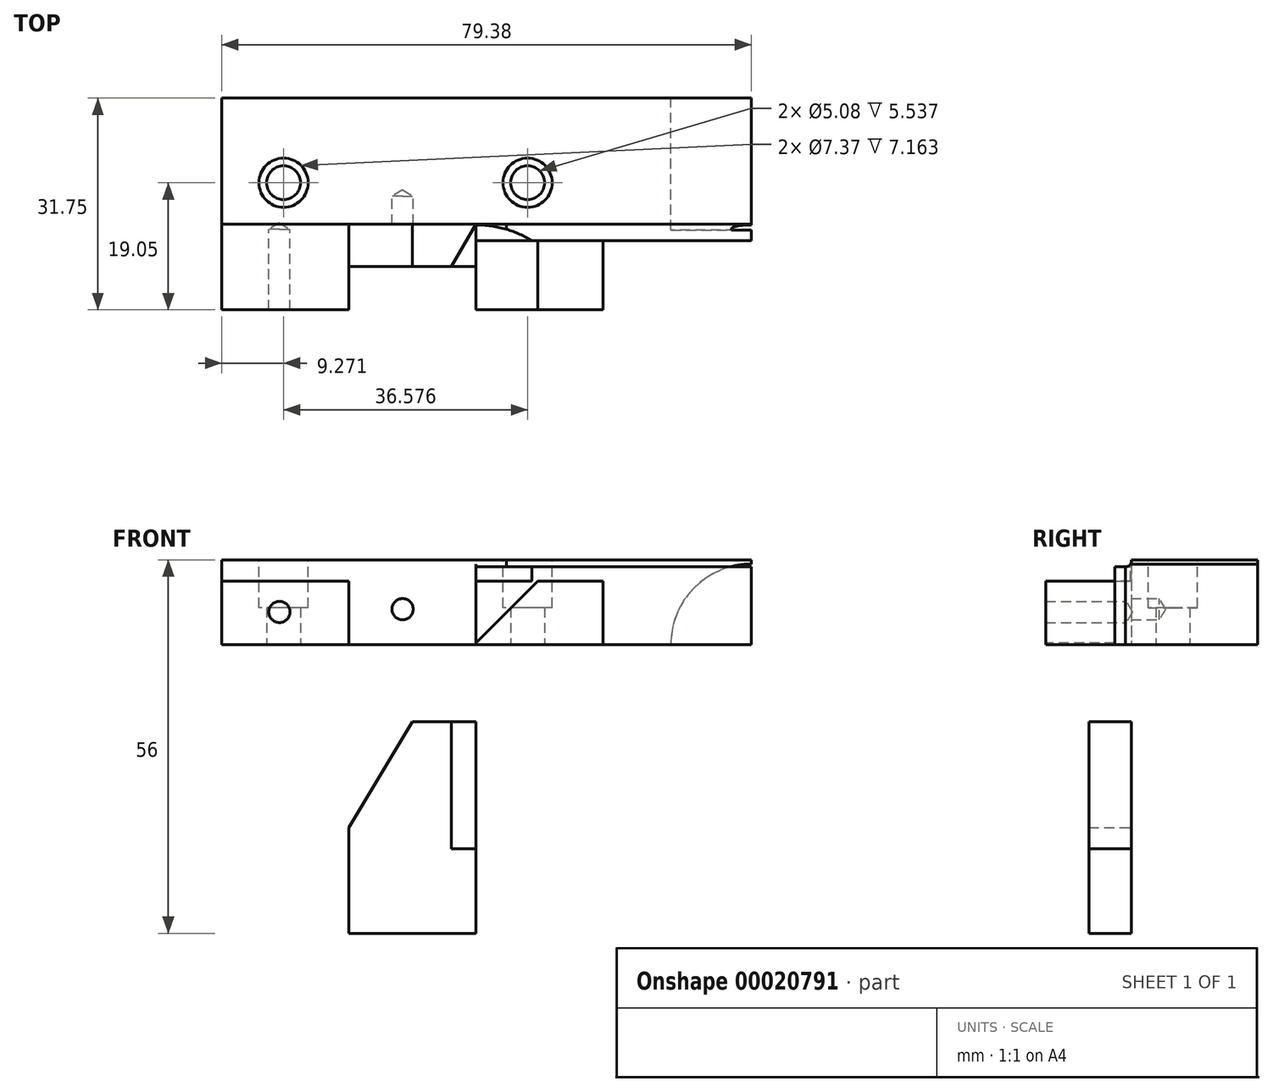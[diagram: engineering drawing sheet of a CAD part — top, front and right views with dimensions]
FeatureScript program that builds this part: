
annotation { "Feature Type Name" : "Feature", "Feature Type Description" : "" }
export const myFeature = defineFeature(function(context is Context, id is Id, definition is map)
    precondition{}
    {
        {
            var Q0;
            Q0=qCreatedBy(makeId("Top.planeOp"),FACE);
            var sketch = newSketch(context, id + "F0", { "sketchPlane" : qUnion([Q0])});
            skLineSegment(sketch, "E0", {"start": v(0, 0) * mm, "end": v(0, -31.75) * mm});
            skLineSegment(sketch, "E1", {"start": v(0, -31.75) * mm, "end": v(19.05, -31.75) * mm});
            skLineSegment(sketch, "E2", {"start": v(19.05, -31.75) * mm, "end": v(19.05, -18.92) * mm});
            skLineSegment(sketch, "E3", {"start": v(19.05, -18.92) * mm, "end": v(38.1, -18.92) * mm});
            skLineSegment(sketch, "E4", {"start": v(38.1, -18.92) * mm, "end": v(38.1, -31.75) * mm});
            skLineSegment(sketch, "E5", {"start": v(38.1, -31.75) * mm, "end": v(57.15, -31.75) * mm});
            skLineSegment(sketch, "E6", {"start": v(57.15, -31.75) * mm, "end": v(57.15, -21.39) * mm});
            skLineSegment(sketch, "E7", {"start": v(57.15, -21.39) * mm, "end": v(79.38, -21.39) * mm});
            skLineSegment(sketch, "E8", {"start": v(79.38, -21.39) * mm, "end": v(79.38, 0) * mm});
            skLineSegment(sketch, "E9", {"start": v(79.38, 0) * mm, "end": v(0, 0) * mm});
            skSolve(sketch);
        }
        {
            var Q0;
            Q0 = qSketchRegion(id + "F0", true);
            extrude(context, id + "F1", {"entities" : qUnion([Q0]), "depth" : 12.7 * mm});
        }
        {
            var Q0;
            Q0=makeQuery(id+"F1.opExtrude","CAP_FACE",FACE,{"disambiguationData":[OSD([sQuery(id+"F0.wireOp",EDGE,"E0"),sQuery(id+"F0.wireOp",EDGE,"E1"),sQuery(id+"F0.wireOp",EDGE,"E2"),sQuery(id+"F0.wireOp",EDGE,"E3"),sQuery(id+"F0.wireOp",EDGE,"E4"),sQuery(id+"F0.wireOp",EDGE,"E5"),sQuery(id+"F0.wireOp",EDGE,"E6"),sQuery(id+"F0.wireOp",EDGE,"E7"),sQuery(id+"F0.wireOp",EDGE,"E8"),sQuery(id+"F0.wireOp",EDGE,"E9")])],"isStart":false});
            var sketch = newSketch(context, id + "F2", { "sketchPlane" : qUnion([Q0])});
            skLineSegment(sketch, "E10.bottom", {"start": v(0, -31.75) * mm, "end": v(19.05, -31.75) * mm});
            skLineSegment(sketch, "E10.top", {"start": v(0, -18.92) * mm, "end": v(19.05, -18.92) * mm});
            skLineSegment(sketch, "E10.left", {"start": v(0, -31.75) * mm, "end": v(0, -18.92) * mm});
            skLineSegment(sketch, "E10.right", {"start": v(19.05, -31.75) * mm, "end": v(19.05, -18.92) * mm});
            skSolve(sketch);
        }
        {
            var Q0;
            Q0 = qSketchRegion(id + "F2", true);
            extrude(context, id + "F3", {"entities" : qUnion([Q0]), "operationType" : NewBodyOperationType.REMOVE, "oppositeDirection" : true, "depth" : 3.17 * mm});
        }
        {
            var Q0;
            Q0=makeQuery(id+"F1.opExtrude","CAP_FACE",FACE,{"disambiguationData":[OSD([sQuery(id+"F0.wireOp",EDGE,"E0"),sQuery(id+"F0.wireOp",EDGE,"E1"),sQuery(id+"F0.wireOp",EDGE,"E2"),sQuery(id+"F0.wireOp",EDGE,"E3"),sQuery(id+"F0.wireOp",EDGE,"E4"),sQuery(id+"F0.wireOp",EDGE,"E5"),sQuery(id+"F0.wireOp",EDGE,"E6"),sQuery(id+"F0.wireOp",EDGE,"E7"),sQuery(id+"F0.wireOp",EDGE,"E8"),sQuery(id+"F0.wireOp",EDGE,"E9")])],"isStart":false});
            var sketch = newSketch(context, id + "F4", { "sketchPlane" : qUnion([Q0])});
            skLineSegment(sketch, "E11.bottom", {"start": v(38.1, -31.75) * mm, "end": v(57.15, -31.75) * mm});
            skLineSegment(sketch, "E11.top", {"start": v(38.1, -21.39) * mm, "end": v(57.15, -21.39) * mm});
            skLineSegment(sketch, "E11.left", {"start": v(38.1, -31.75) * mm, "end": v(38.1, -21.39) * mm});
            skLineSegment(sketch, "E11.right", {"start": v(57.15, -31.75) * mm, "end": v(57.15, -21.39) * mm});
            skSolve(sketch);
        }
        {
            var Q0;
            Q0 = qSketchRegion(id + "F4", true);
            extrude(context, id + "F5", {"entities" : qUnion([Q0]), "operationType" : NewBodyOperationType.REMOVE, "oppositeDirection" : true, "depth" : 3.17 * mm});
        }
        {
            var Q0;
            Q0=makeQuery(id+"F1.opExtrude","SWEPT_FACE",FACE,{"disambiguationData":[OSD([sQuery(id+"F0.wireOp",EDGE,"E5")])]});
            var sketch = newSketch(context, id + "F6", { "sketchPlane" : qUnion([Q0])});
            skLineSegment(sketch, "E12", {"start": v(38.1, 0.25) * mm, "end": v(47.37, 9.53) * mm});
            skLineSegment(sketch, "E13", {"start": v(47.37, 9.53) * mm, "end": v(38.1, 9.53) * mm});
            skLineSegment(sketch, "E14", {"start": v(38.1, 9.53) * mm, "end": v(38.1, 0.25) * mm});
            skLineSegment(sketch, "E15", {"start": v(41.97, 0.25) * mm, "end": v(33.92, 0.25) * mm, "construction": true});
            skSolve(sketch);
        }
        {
            var Q0;
            Q0 = qSketchRegion(id + "F6", true);
            extrude(context, id + "F7", {"entities" : qUnion([Q0]), "operationType" : NewBodyOperationType.REMOVE, "oppositeDirection" : true, "depth" : 10.36 * mm});
        }
        {
            var Q0;
            Q0=makeQuery(id+"F1.opExtrude","CAP_FACE",FACE,{"disambiguationData":[OSD([sQuery(id+"F0.wireOp",EDGE,"E0"),sQuery(id+"F0.wireOp",EDGE,"E1"),sQuery(id+"F0.wireOp",EDGE,"E2"),sQuery(id+"F0.wireOp",EDGE,"E3"),sQuery(id+"F0.wireOp",EDGE,"E4"),sQuery(id+"F0.wireOp",EDGE,"E5"),sQuery(id+"F0.wireOp",EDGE,"E6"),sQuery(id+"F0.wireOp",EDGE,"E7"),sQuery(id+"F0.wireOp",EDGE,"E8"),sQuery(id+"F0.wireOp",EDGE,"E9")])],"isStart":false});
            var sketch = newSketch(context, id + "F8", { "sketchPlane" : qUnion([Q0])});
            skLineSegment(sketch, "E16.bottom", {"start": v(38.1, -21.39) * mm, "end": v(79.38, -21.39) * mm});
            skLineSegment(sketch, "E16.top", {"start": v(38.1, -18.92) * mm, "end": v(79.38, -18.92) * mm});
            skLineSegment(sketch, "E16.left", {"start": v(38.1, -21.39) * mm, "end": v(38.1, -18.92) * mm});
            skLineSegment(sketch, "E16.right", {"start": v(79.38, -21.39) * mm, "end": v(79.38, -18.92) * mm});
            skLineSegment(sketch, "E17.bottom", {"start": v(38.1, -18.92) * mm, "end": v(38.1, -18.92) * mm});
            skLineSegment(sketch, "E17.top", {"start": v(38.1, -18.92) * mm, "end": v(38.1, -18.92) * mm});
            skLineSegment(sketch, "E17.left", {"start": v(38.1, -18.92) * mm, "end": v(38.1, -18.92) * mm});
            skLineSegment(sketch, "E17.right", {"start": v(38.1, -18.92) * mm, "end": v(38.1, -18.92) * mm});
            skSolve(sketch);
        }
        {
            var Q0;
            Q0 = qSketchRegion(id + "F8", true);
            extrude(context, id + "F9", {"entities" : qUnion([Q0]), "operationType" : NewBodyOperationType.REMOVE, "oppositeDirection" : true, "depth" : 1.02 * mm});
        }
        {
            var Q0;
            Q0=makeQuery(id+"F1.opExtrude","SWEPT_FACE",FACE,{"disambiguationData":[OSD([sQuery(id+"F0.wireOp",EDGE,"E9")])]});
            var sketch = newSketch(context, id + "F10", { "sketchPlane" : qUnion([Q0])});
            skLineSegment(sketch, "E18", {"start": v(-85.5, 11.94) * mm, "end": v(-73.35, 11.94) * mm, "construction": true});
            skLineSegment(sketch, "E19", {"start": v(-67.1, -7.76) * mm, "end": v(-67.1, 3.98) * mm, "construction": true});
            skCircle(sketch, "E20", {"center": v(-79.38, 0) * mm, "radius": 12.07 * mm});
            skSolve(sketch);
        }
        {
            var Q0;
            Q0 = qSketchRegion(id + "F10", true);
            extrude(context, id + "F11", {"entities" : qUnion([Q0]), "operationType" : NewBodyOperationType.REMOVE, "oppositeDirection" : true, "depth" : 19.8 * mm});
        }
        {
            var Q0;
            Q0=makeQuery(id+"F9.boolean.opBoolean","COPY",FACE,{"derivedFrom":makeQuery(id+"F9.opExtrude","CAP_FACE",FACE,{"disambiguationData":[OSD([sQuery(id+"F8.wireOp",EDGE,"E16.bottom"),sQuery(id+"F8.wireOp",EDGE,"E16.top"),sQuery(id+"F8.wireOp",EDGE,"E16.left"),sQuery(id+"F8.wireOp",EDGE,"E16.right")])],"isStart":false})});
            var sketch = newSketch(context, id + "F12", { "sketchPlane" : qUnion([Q0])});
            skPoint(sketch, "E21.first.point", {"position": v(38.1, -18.92) * mm});
            skPoint(sketch, "E21.second.point", {"position": v(38.1, -52.5) * mm});
            skPoint(sketch, "E21.third.point", {"position": v(21.31, -36.1) * mm});
            skLineSegment(sketch, "E22", {"start": v(55.27, -29.27) * mm, "end": v(55.27, -36.3) * mm, "construction": true});
            skLineSegment(sketch, "E23", {"start": v(46.5, -17.5) * mm, "end": v(46.5, -27.25) * mm, "construction": true});
            skLineSegment(sketch, "E24", {"start": v(64.56, -31.75) * mm, "end": v(33.9, -31.75) * mm, "construction": true});
            skLineSegment(sketch, "E25", {"start": v(28.67, -21.39) * mm, "end": v(81.35, -21.39) * mm, "construction": true});
            skPoint(sketch, "E26.second.point", {"position": v(55.27, -31.75) * mm});
            skPoint(sketch, "E26.third.point", {"position": v(46.5, -21.39) * mm});
            skLineSegment(sketch, "E27", {"start": v(34, -19.02) * mm, "end": v(43.83, -19.02) * mm, "construction": true});
            skLineSegment(sketch, "E28", {"start": v(38.1, -20.68) * mm, "end": v(38.1, -16.21) * mm, "construction": true});
            skCircle(sketch, "E29", {"center": v(38.1, -35.17) * mm, "radius": 16.14 * mm});
            skSolve(sketch);
        }
        {
            var Q0;
            Q0 = qSketchRegion(id + "F12", true);
            var Q1;
            Q1=makeQuery(id+"F5.boolean.opBoolean","COPY",FACE,{"derivedFrom":makeQuery(id+"F5.opExtrude","CAP_FACE",FACE,{"disambiguationData":[OSD([sQuery(id+"F4.wireOp",EDGE,"E11.bottom"),sQuery(id+"F4.wireOp",EDGE,"E11.top"),sQuery(id+"F4.wireOp",EDGE,"E11.left"),sQuery(id+"F4.wireOp",EDGE,"E11.right")])],"isStart":false})});
            extrude(context, id + "F13", {"entities" : qUnion([Q0]), "operationType" : NewBodyOperationType.REMOVE, "endBound" : BoundingType.UP_TO_SURFACE, "oppositeDirection" : true, "endBoundEntityFace" : qUnion([Q1]), "depth" : 25.4 * mm});
        }
        {
            var Q0;
            Q0=makeQuery(id+"F1.opExtrude","CAP_FACE",FACE,{"disambiguationData":[OSD([sQuery(id+"F0.wireOp",EDGE,"E0"),sQuery(id+"F0.wireOp",EDGE,"E1"),sQuery(id+"F0.wireOp",EDGE,"E2"),sQuery(id+"F0.wireOp",EDGE,"E3"),sQuery(id+"F0.wireOp",EDGE,"E4"),sQuery(id+"F0.wireOp",EDGE,"E5"),sQuery(id+"F0.wireOp",EDGE,"E6"),sQuery(id+"F0.wireOp",EDGE,"E7"),sQuery(id+"F0.wireOp",EDGE,"E8"),sQuery(id+"F0.wireOp",EDGE,"E9")])],"isStart":true});
            var sketch = newSketch(context, id + "F14", { "sketchPlane" : qUnion([Q0])});
            skCircle(sketch, "E30", {"center": v(9.27, 12.7) * mm, "radius": 2.54 * mm});
            skCircle(sketch, "E31", {"center": v(45.85, 12.7) * mm, "radius": 2.54 * mm});
            skSolve(sketch);
        }
        {
            var Q0;
            Q0 = qSketchRegion(id + "F14", true);
            extrude(context, id + "F15", {"entities" : qUnion([Q0]), "operationType" : NewBodyOperationType.REMOVE, "endBound" : BoundingType.THROUGH_ALL, "oppositeDirection" : true, "depth" : 25.4 * mm});
        }
        {
            var Q0;
            Q0=makeQuery(id+"F1.opExtrude","CAP_FACE",FACE,{"disambiguationData":[OSD([sQuery(id+"F0.wireOp",EDGE,"E0"),sQuery(id+"F0.wireOp",EDGE,"E1"),sQuery(id+"F0.wireOp",EDGE,"E2"),sQuery(id+"F0.wireOp",EDGE,"E3"),sQuery(id+"F0.wireOp",EDGE,"E4"),sQuery(id+"F0.wireOp",EDGE,"E5"),sQuery(id+"F0.wireOp",EDGE,"E6"),sQuery(id+"F0.wireOp",EDGE,"E7"),sQuery(id+"F0.wireOp",EDGE,"E8"),sQuery(id+"F0.wireOp",EDGE,"E9")])],"isStart":false});
            var sketch = newSketch(context, id + "F16", { "sketchPlane" : qUnion([Q0])});
            skCircle(sketch, "E32", {"center": v(9.27, -12.7) * mm, "radius": 3.68 * mm});
            skCircle(sketch, "E33", {"center": v(45.85, -12.7) * mm, "radius": 3.68 * mm});
            skSolve(sketch);
        }
        {
            var Q0;
            Q0 = qSketchRegion(id + "F16", true);
            extrude(context, id + "F17", {"entities" : qUnion([Q0]), "operationType" : NewBodyOperationType.REMOVE, "oppositeDirection" : true, "depth" : 7.16 * mm});
        }
        {
            var Q0;
            Q0=makeQuery(id+"F1.opExtrude","SWEPT_FACE",FACE,{"disambiguationData":[OSD([sQuery(id+"F0.wireOp",EDGE,"E1")])]});
            var sketch = newSketch(context, id + "F18", { "sketchPlane" : qUnion([Q0])});
            skCircle(sketch, "E34", {"center": v(8.66, 4.9) * mm, "radius": 1.57 * mm});
            skSolve(sketch);
        }
        {
            var Q0;
            Q0=sQuery(id+"F18.wireOp",VERTEX,"E34.center");
            var Q1;
            Q1=makeQuery(id+"F1.opExtrude","SWEPT_BODY",BODY,{"disambiguationData":[OSD([sQuery(id+"F0.wireOp",EDGE,"E0"),sQuery(id+"F0.wireOp",EDGE,"E1"),sQuery(id+"F0.wireOp",EDGE,"E2"),sQuery(id+"F0.wireOp",EDGE,"E3"),sQuery(id+"F0.wireOp",EDGE,"E4"),sQuery(id+"F0.wireOp",EDGE,"E5"),sQuery(id+"F0.wireOp",EDGE,"E6"),sQuery(id+"F0.wireOp",EDGE,"E7"),sQuery(id+"F0.wireOp",EDGE,"E8"),sQuery(id+"F0.wireOp",EDGE,"E9")])]});
            hole(context, id + "F19", {"style" : HoleStyle.SIMPLE, "holeDiameter" : 3.17 * mm, "endStyle" : HoleEndStyle.BLIND, "holeDepth" : 12.06 * mm, "locations" : qUnion([Q0]), "scope" : qUnion([Q1])});
        }
        {
            var Q0;
            Q0=makeQuery(id+"F9.boolean.opBoolean","MERGE",FACE,{"derivedFrom":[makeQuery(id+"F3.boolean.opBoolean","MERGE",FACE,{"derivedFrom":[makeQuery(id+"F1.opExtrude","SWEPT_FACE",FACE,{"disambiguationData":[OSD([sQuery(id+"F0.wireOp",EDGE,"E3")])]}),makeQuery(id+"F3.opExtrude","SWEPT_FACE",FACE,{"disambiguationData":[OSD([sQuery(id+"F2.wireOp",EDGE,"E10.top")])]})]}),makeQuery(id+"F9.opExtrude","SWEPT_FACE",FACE,{"disambiguationData":[OSD([sQuery(id+"F8.wireOp",EDGE,"E16.top")])]})]});
            var sketch = newSketch(context, id + "F20", { "sketchPlane" : qUnion([Q0])});
            skCircle(sketch, "E35", {"center": v(27.11, 5.3) * mm, "radius": 1.33 * mm});
            skSolve(sketch);
        }
        {
            var Q0;
            Q0=sQuery(id+"F20.wireOp",VERTEX,"E35.center");
            var Q1;
            Q1=makeQuery(id+"F1.opExtrude","SWEPT_BODY",BODY,{"disambiguationData":[OSD([sQuery(id+"F0.wireOp",EDGE,"E0"),sQuery(id+"F0.wireOp",EDGE,"E1"),sQuery(id+"F0.wireOp",EDGE,"E2"),sQuery(id+"F0.wireOp",EDGE,"E3"),sQuery(id+"F0.wireOp",EDGE,"E4"),sQuery(id+"F0.wireOp",EDGE,"E5"),sQuery(id+"F0.wireOp",EDGE,"E6"),sQuery(id+"F0.wireOp",EDGE,"E7"),sQuery(id+"F0.wireOp",EDGE,"E8"),sQuery(id+"F0.wireOp",EDGE,"E9")])]});
            hole(context, id + "F21", {"style" : HoleStyle.SIMPLE, "holeDiameter" : 3.17 * mm, "endStyle" : HoleEndStyle.BLIND, "holeDepth" : 4.2 * mm, "locations" : qUnion([Q0]), "scope" : qUnion([Q1])});
        }
        {
            var Q0;
            Q0=makeQuery(id+"F9.boolean.opBoolean","COPY",EDGE,{"derivedFrom":makeQuery(id+"F9.opExtrude","CAP_EDGE",EDGE,{"disambiguationData":[OSD([sQuery(id+"F8.wireOp",EDGE,"E16.top")])],"isStart":false})});
            fillet(context, id + "F22", {"entities" : qUnion([Q0]), "radius" : 0.76 * mm, "tangentPropagation" : true, "allowEdgeOverflow" : false});
        }
        {
            var Q0;
            Q0 = qSketchRegion(id + "F12", true);
            extrude(context, id + "F23", {"entities" : qUnion([Q0]), "operationType" : NewBodyOperationType.REMOVE, "depth" : 25.4 * mm});
        }
        {
            var Q0;
            Q0=makeQuery(id+"F9.boolean.opBoolean","MERGE",FACE,{"derivedFrom":[makeQuery(id+"F3.boolean.opBoolean","MERGE",FACE,{"derivedFrom":[makeQuery(id+"F1.opExtrude","SWEPT_FACE",FACE,{"disambiguationData":[OSD([sQuery(id+"F0.wireOp",EDGE,"E3")])]}),makeQuery(id+"F3.opExtrude","SWEPT_FACE",FACE,{"disambiguationData":[OSD([sQuery(id+"F2.wireOp",EDGE,"E10.top")])]})]}),makeQuery(id+"F9.opExtrude","SWEPT_FACE",FACE,{"disambiguationData":[OSD([sQuery(id+"F8.wireOp",EDGE,"E16.top")])]})]});
            var sketch = newSketch(context, id + "F24", { "sketchPlane" : qUnion([Q0])});
            skLineSegment(sketch, "E36", {"start": v(19.05, -43.3) * mm, "end": v(38.1, -43.3) * mm});
            skLineSegment(sketch, "E37", {"start": v(38.1, -43.3) * mm, "end": v(38.1, -11.55) * mm});
            skLineSegment(sketch, "E38", {"start": v(38.1, -11.55) * mm, "end": v(28.58, -11.55) * mm});
            skLineSegment(sketch, "E39", {"start": v(28.58, -11.55) * mm, "end": v(19.05, -27.43) * mm});
            skLineSegment(sketch, "E40", {"start": v(19.05, -27.43) * mm, "end": v(19.05, -43.3) * mm});
            skSolve(sketch);
        }
        {
            var Q0;
            Q0 = qSketchRegion(id + "F24", true);
            extrude(context, id + "F25", {"entities" : qUnion([Q0]), "depth" : 6.35 * mm});
        }
        {
            var Q0;
            Q0=makeQuery(id+"F25.opExtrude","SWEPT_FACE",FACE,{"disambiguationData":[OSD([sQuery(id+"F24.wireOp",EDGE,"E38")])]});
            var sketch = newSketch(context, id + "F26", { "sketchPlane" : qUnion([Q0])});
            skLineSegment(sketch, "E41", {"start": v(38.1, -18.92) * mm, "end": v(34.43, -25.27) * mm});
            skLineSegment(sketch, "E42", {"start": v(34.43, -25.27) * mm, "end": v(38.1, -25.27) * mm});
            skLineSegment(sketch, "E43", {"start": v(38.1, -25.27) * mm, "end": v(38.1, -18.92) * mm});
            skSolve(sketch);
        }
        {
            var Q0;
            Q0 = qSketchRegion(id + "F26", true);
            extrude(context, id + "F27", {"entities" : qUnion([Q0]), "operationType" : NewBodyOperationType.REMOVE, "oppositeDirection" : true, "depth" : 19.05 * mm});
        }
    });
